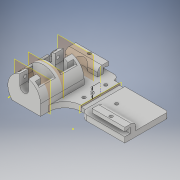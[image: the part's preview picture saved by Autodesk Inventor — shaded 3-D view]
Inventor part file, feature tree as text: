
AUTODESK INVENTOR PART (.ipt)
format: ipt  version: 2018 (Build 220112000, 112)  size: 392,704 bytes
history: native  units: in
note: dims shown in document units (in); Inventor stores cm internally (conversion verified against a paired STEP export)
features: sketch x15, extrude x14, plane x5, fillet x3, mirror x2, other x1, pattern_circular x1
ambient origin geometry x8: Origin, YZ Plane, XZ Plane, XY Plane, X Axis, Y Axis, Z Axis, Center Point
bodies: Solid1 (feature_tree)
feature tree (41):
  extrude  "Extrusion1"  Depth=0.1969in TaperAngle=0.0deg
  extrude  "Extrusion2"  Depth=1.378in TaperAngle=0.0deg
  plane  "Work Plane1"
  extrude  "Extrusion3"  Depth=0.3937in
  extrude  "Extrusion4"  Depth=0.748in
  extrude  "Extrusion5"  Depth=0.3937in
  plane  "Work Plane2"
  fillet  "Fillet1"  Radius=0.1181in
  mirror  "Mirror1"
  plane  "Work Plane3"
  extrude  "Extrusion6"  Depth=0.1969in TaperAngle=0.0deg
  extrude  "Extrusion7"  Depth=0.0394in
  extrude  "Extrusion8"  Depth=0.1181in TaperAngle=0.0deg
  plane  "Work Plane4"
  sketch  "Sketch9"  dims[d25=0.315in d27=0.0394in]
  other  "Work Axis1"
  extrude  "Extrusion10"  [1 undecoded]
  mirror  "Mirror4"
  extrude  "Extrusion12"  Depth=0.2953in
  fillet  "Fillet3"  Radius=0.1575in
  sketch  "Sketch15"  dims[d31=-0.689in d32=0.0394in d33=-1.7717in]
  pattern_circular  "Circular Pattern3"  Count=3  [1 undecoded]
  extrude  "Extrusion15"  Depth=0.0984in
  plane  "Work Plane5"
  fillet  "Fillet7"  Radius=0.1181in
  sketch  "Sketch19"  dims[d37=0.0in]
  extrude  "Extrusion18"  Depth=0.3937in
  extrude  "Extrusion20"  Depth=0.7874in
  sketch  "Sketch23"  dims[d44=0.1969in d45=0.0in d46=0.3937in]
  extrude  "Extrusion21"  Depth=0.3937in
  sketch  "Sketch1"  dims[d6=1.1811in d8=0.1969in d9=0.0in]
  sketch  "Sketch2"  dims[d10=0.1969in d11=1.378in d12=0.0in]
  sketch  "Sketch3"  dims[d13=-0.1969in d14=0.3937in]
  sketch  "Sketch4"  dims[d16=0.374in d17=0.748in]
  sketch  "Sketch5"  dims[d18=0.3937in d19=0.0in d20=0.315in d21=0.1181in]
  sketch  "Sketch6"  dims[d22=0.0787in d23=0.1969in d24=0.0in]
  sketch  "Sketch10"  dims[d28=0.1181in d29=0.1181in d30=0.0in]
  sketch  "Sketch16"  dims[d34=0.3937in d35=0.2953in d36=0.1575in]
  sketch  "Sketch20"  dims[d38=0.1969in d39=1.1811in d40=0.0in]
  sketch  "Sketch22"  dims[d41=1.1977in d42=0.0984in d43=0.1181in]
  sketch  "Sketch24"  dims[d47=0.3937in d48=0.7874in d49=0.1181in d50=0.1181in d51=0.1181in d52=0.1969in d53=0.0in d54=-1.7717in d55=0.3937in d60=0.0787in d63=0.0984in d64=0.0in d68=0.1969in d69=0.0in d86=0.0787in d87=0.5906in d89=0.1378in d91=0.7874in d92=360.0deg d95=0.5906in d96=0.2953in d97=0.0in d116=0.3937in d117=0.1969in d118=0.3937in d119=0.0in d123=0.3937in d124=0.0in d125=0.1969in d126=0.0591in d127=0.3937in d128=0.0in]
note: 2 required parameter values undecoded (feature->parameter linkage not recoverable at this tier; creation-order binding heuristic only, values carry confidence <= 0.55)
